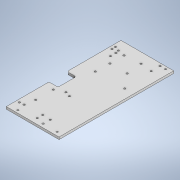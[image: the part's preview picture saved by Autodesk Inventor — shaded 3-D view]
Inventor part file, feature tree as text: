
AUTODESK INVENTOR PART (.ipt)
format: ipt  version: 2021 (Build 250183000, 183)  size: 229,376 bytes
history: native  units: mm
features: sketch x12, hole x10, extrude x2, fillet x2
ambient origin geometry x8: Origin, YZ Plane, XZ Plane, XY Plane, X Axis, Y Axis, Z Axis, Center Point
bodies: Solid1 (feature_tree)
feature tree (26):
  extrude  "Extrusion1"  Depth=252.75mm
  hole  "Hole1"  [1 undecoded]
  hole  "Hole2"  [1 undecoded]
  hole  "Hole3"  [1 undecoded]
  hole  "Hole5"  [1 undecoded]
  hole  "Hole6"  [1 undecoded]
  hole  "Hole7"  [1 undecoded]
  hole  "Hole8"  [1 undecoded]
  hole  "Hole9"  [1 undecoded]
  hole  "Hole10"  [1 undecoded]
  hole  "Hole11"  [1 undecoded]
  extrude  "Extrusion2"  Depth=2.0mm
  fillet  "Fillet1"  Radius=24.0mm
  fillet  "Fillet2"  Radius=12.554232mm
  sketch  "Sketch1"  dims[d0=116.2mm d1=252.75mm]
  sketch  "Sketch2"  dims[d2=5.0mm d3=0.0mm d4=8.0mm]
  sketch  "Sketch3"  dims[d5=6.0mm d6=12.0mm]
  sketch  "Sketch4"  dims[d7=12.0mm d8=12.0mm]
  sketch  "Sketch6"  dims[d9=31.0mm]
  sketch  "Sketch7"  dims[d10=3.8mm d11=6.0mm d12=4.0mm d13=2.0mm d14=90.0deg d15=8.0mm d16=20.594885mm d17=60.0mm]
  sketch  "Sketch8"  dims[d19=12.0mm]
  sketch  "Sketch9"  dims[d20=3.8mm d21=6.0mm d22=4.0mm d23=2.0mm d24=90.0deg d25=8.0mm d26=20.594885mm d27=12.0mm]
  sketch  "Sketch10"  dims[d28=53.75mm d29=18.5mm]
  sketch  "Sketch11"  dims[d30=12.0mm d31=24.0mm]
  sketch  "Sketch12"  dims[d32=3.8mm d33=6.0mm d34=4.0mm d35=2.0mm d36=90.0deg d37=8.0mm d38=20.594885mm d50=22.5mm]
  sketch  "Sketch13"  dims[d51=16.7mm d52=66.7mm d53=3.8mm d54=6.0mm d55=4.0mm d56=2.0mm d57=90.0deg d58=8.0mm d59=20.594885mm d60=163.513mm d61=49.922mm d64=24.0mm d65=3.8mm d66=6.0mm d67=4.0mm d68=2.0mm d69=90.0deg d70=8.0mm d71=20.594885mm d73=12.554232mm d74=23.25mm d75=16.0mm d76=73.5mm d77=3.8mm d78=6.0mm d79=4.0mm d80=2.0mm d81=90.0deg d82=8.0mm d83=20.594885mm d84=25.5mm d85=24.0mm d86=84.0mm d87=3.8mm d88=6.0mm d89=4.0mm d90=2.0mm d91=90.0deg d92=8.0mm d93=20.594885mm d94=56.5mm d95=84.0mm d96=46.0mm d97=26.5mm d98=6.7mm d99=6.5mm d100=18.75mm d101=211.75mm d102=3.8mm d103=6.0mm d104=4.0mm d105=2.0mm d106=90.0deg d107=8.0mm d108=20.594885mm d109=6.0mm d110=19.5mm d111=39.0mm d112=39.0mm d113=3.8mm d114=6.0mm d115=4.0mm d116=2.0mm d117=90.0deg d118=8.0mm d119=20.594885mm d120=88.0mm d121=20.0mm d122=85.0mm d123=3.8mm d124=6.0mm d125=4.0mm d126=2.0mm d127=90.0deg d128=8.0mm d129=20.594885mm d130=114.0mm d131=40.0mm d132=40.0mm d133=0.0mm d134=0.0mm d135=4.0mm d136=2.0mm]
note: 10 required parameter values undecoded (feature->parameter linkage not recoverable at this tier; creation-order binding heuristic only, values carry confidence <= 0.55)
